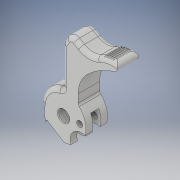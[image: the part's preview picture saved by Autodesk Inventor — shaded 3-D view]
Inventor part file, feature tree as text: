
AUTODESK INVENTOR PART (.ipt)
format: ipt  version: 2018.3 (Build 223284000, 284)  size: 342,016 bytes
history: native  units: in
note: dims shown in document units (in); Inventor stores cm internally (conversion verified against a paired STEP export)
features: extrude x3, sketch x1, fillet x1, chamfer x1
ambient origin geometry x8: Origin, YZ Plane, XZ Plane, XY Plane, X Axis, Y Axis, Z Axis, Center Point
bodies: Solid1 (feature_tree)
feature tree (6):
  sketch  "Sketch1"  dims[d0=0.64in d1=0.1575in d6=0.018in d7=0.232in d8=0.085in d9=0.242in d10=0.259in d11=0.332in d12=0.8435in d13=0.109in d14=0.225in d15=0.268in d16=0.754in d17=0.0687in d19=0.081in d20=0.309in d21=0.0in d22=0.116in d23=0.0in d24=1.0in d25=0.0in d27=0.38in d28=0.013in d29=0.222in d30=0.84in d31=0.8108in d32=0.432in d33=0.06in d34=0.05in d35=0.38in d36=0.5in d37=0.55in d38=0.72in d39=0.96in d40=0.12in d41=1.84in d42=0.92in d45=30.0deg d46=0.2in d47=0.015in d48=0.02in d49=0.02in d50=0.03in d51=0.02in d52=0.02in d53=0.02in d54=0.03in d55=0.03in d56=0.03in d57=0.06in d58=0.01in d59=0.125in d60=60.0deg]
  extrude  "Extrusion1"  Depth=0.309in
  extrude  "Extrusion2"  Depth=0.309in
  extrude  "Extrusion3"  Depth=0.309in
  fillet  "Fillet1"  Radius=0.085in
  chamfer  "Chamfer1"  Distance=0.242in
